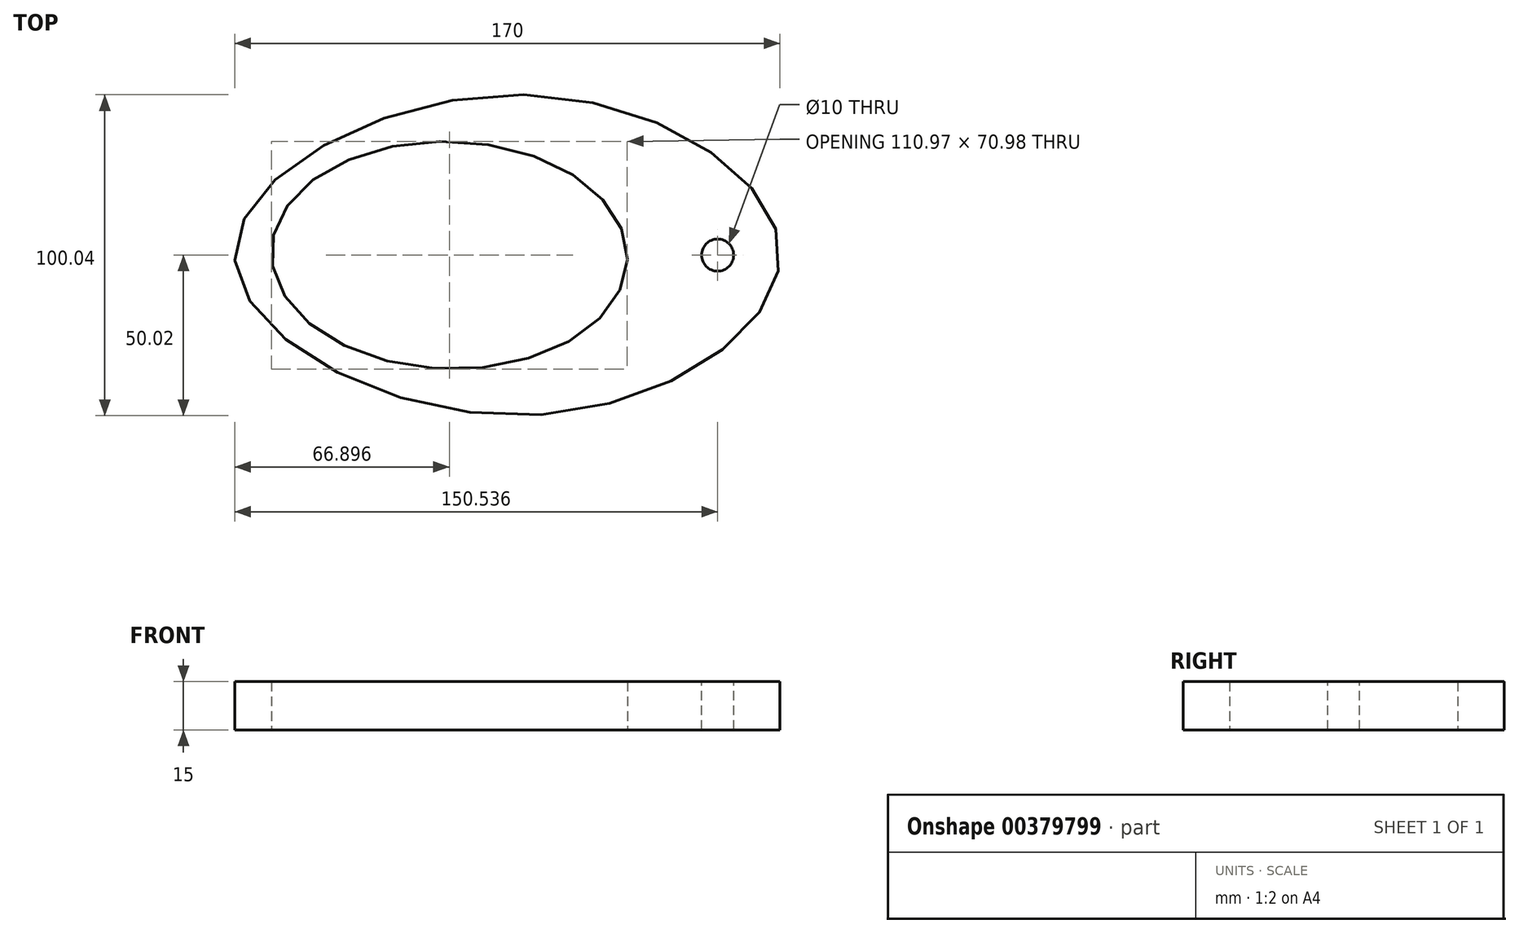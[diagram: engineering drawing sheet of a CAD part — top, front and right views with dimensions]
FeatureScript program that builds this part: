
annotation { "Feature Type Name" : "Feature", "Feature Type Description" : "" }
export const myFeature = defineFeature(function(context is Context, id is Id, definition is map)
    precondition{}
    {
        {
            var Q0;
            Q0=qCreatedBy(makeId("Top.planeOp"),FACE);
            var sketch = newSketch(context, id + "F0", { "sketchPlane" : qUnion([Q0])});
            skFitSpline(sketch, "E0", {"points": [v(0, 50) * mm, v(80, 0) * mm, v(0, -50) * mm, v(-90, 0) * mm, v(0, 50) * mm]});
            skSolve(sketch);
        }
        {
            var Q0;
            Q0=makeQuery(id+"F0.imprint","IMPRINT",FACE,{"disambiguationData":[TD([[makeQuery(id+"F0.imprint","IMPRINT",EDGE,{"derivedFrom":sQuery(id+"F0.wireOp",EDGE,"E0")}),-1.0]])]});
            extrude(context, id + "F1", {"entities" : qUnion([Q0]), "depth" : 15 * mm});
        }
        {
            var Q0;
            Q0=makeQuery(id+"F1.opExtrude","CAP_FACE",FACE,{"disambiguationData":[OSD([sQuery(id+"F0.wireOp",EDGE,"E0")])],"isStart":true});
            var sketch = newSketch(context, id + "F2", { "sketchPlane" : qUnion([Q0])});
            skCircle(sketch, "E1", {"center": v(0, 0) * mm, "radius": 10 * mm});
            skSolve(sketch);
        }
        {
            var Q0;
            Q0 = qSketchRegion(id + "F2", true);
            extrude(context, id + "F3", {"entities" : qUnion([Q0]), "operationType" : NewBodyOperationType.REMOVE, "oppositeDirection" : true, "depth" : 6 * mm});
        }
        {
            var Q0;
            Q0=makeQuery(id+"F1.opExtrude","CAP_FACE",FACE,{"disambiguationData":[OSD([sQuery(id+"F0.wireOp",EDGE,"E0")])],"isStart":false});
            var sketch = newSketch(context, id + "F4", { "sketchPlane" : qUnion([Q0])});
            skEllipse(sketch, "E2", {"center": v(-23.1, 0) * mm, "majorRadius": 55.5 * mm, "minorRadius": 35.5 * mm, "majorAxis": v(1, -0.02)});
            skSolve(sketch);
        }
        {
            var Q0;
            Q0=makeQuery(id+"F4.imprint","IMPRINT",FACE,{"disambiguationData":[TD([[makeQuery(id+"F4.imprint","IMPRINT",EDGE,{"derivedFrom":sQuery(id+"F4.wireOp",EDGE,"E2")}),1.0]])]});
            extrude(context, id + "F5", {"entities" : qUnion([Q0]), "operationType" : NewBodyOperationType.REMOVE, "oppositeDirection" : true, "depth" : 25 * mm});
        }
        {
            var Q0;
            Q0=makeQuery(id+"F1.opExtrude","CAP_FACE",FACE,{"disambiguationData":[OSD([sQuery(id+"F0.wireOp",EDGE,"E0")])],"isStart":false});
            var sketch = newSketch(context, id + "F6", { "sketchPlane" : qUnion([Q0])});
            skCircle(sketch, "E3", {"center": v(60.54, 0) * mm, "radius": 5 * mm});
            skSolve(sketch);
        }
        {
            var Q0;
            Q0 = qSketchRegion(id + "F6", true);
            extrude(context, id + "F7", {"entities" : qUnion([Q0]), "operationType" : NewBodyOperationType.REMOVE, "oppositeDirection" : true, "depth" : 25 * mm});
        }
    });
